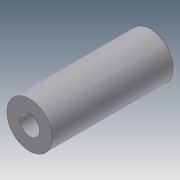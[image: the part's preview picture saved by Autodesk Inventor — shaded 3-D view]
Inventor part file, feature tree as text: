
AUTODESK INVENTOR PART (.ipt)
format: ipt  version: 2020.4 (Build 244396000, 396)  size: 102,912 bytes
history: native  units: in
note: dims shown in document units (in); Inventor stores cm internally (conversion verified against a paired STEP export)
features: extrude x1
ambient origin geometry x8: Origin, YZ Plane, XZ Plane, XY Plane, X Axis, Y Axis, Z Axis, Center Point
bodies: Solid1 (feature_tree)
feature tree (1):
  extrude  "Extrude1"  [1 undecoded]
note: 1 required parameter value undecoded (feature->parameter linkage not recoverable at this tier; creation-order binding heuristic only, values carry confidence <= 0.55)
